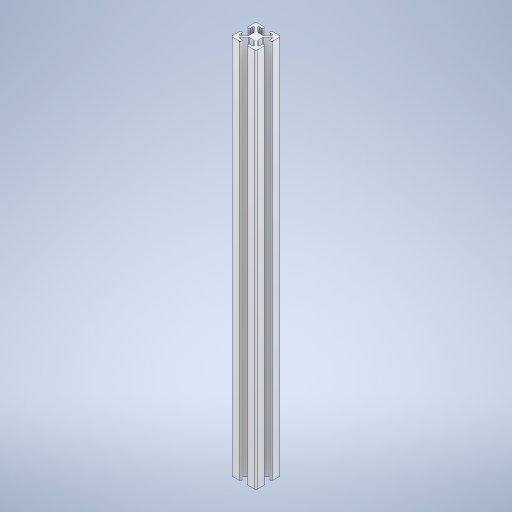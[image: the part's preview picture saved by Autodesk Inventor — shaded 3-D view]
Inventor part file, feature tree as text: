
AUTODESK INVENTOR PART (.ipt)
format: ipt  version: 2024 (Build 280153000, 153)  size: 344,064 bytes
history: native  units: in
note: dims shown in document units (in); Inventor stores cm internally (conversion verified against a paired STEP export)
features: fillet x2, extrude x1, sketch x1
ambient origin geometry x8: Origin, YZ Plane, XZ Plane, XY Plane, X Axis, Y Axis, Z Axis, Center Point
bodies: Solid1 (feature_tree)
feature tree (4):
  extrude  "Extrusion1"  Depth=1.0in
  fillet  "Fillet1"  Radius=0.8in
  fillet  "Fillet2"  Radius=0.8in
  sketch  "Sketch1"  dims[d0=1.0in d1=1.0in d2=0.8in d3=0.8in d4=0.35in d5=0.35in d6=0.125in d7=0.25in d8=0.125in d9=0.25in d10=0.1in d11=0.1in d12=15.35in d13=0.0in d14=0.05in d15=0.025in]
